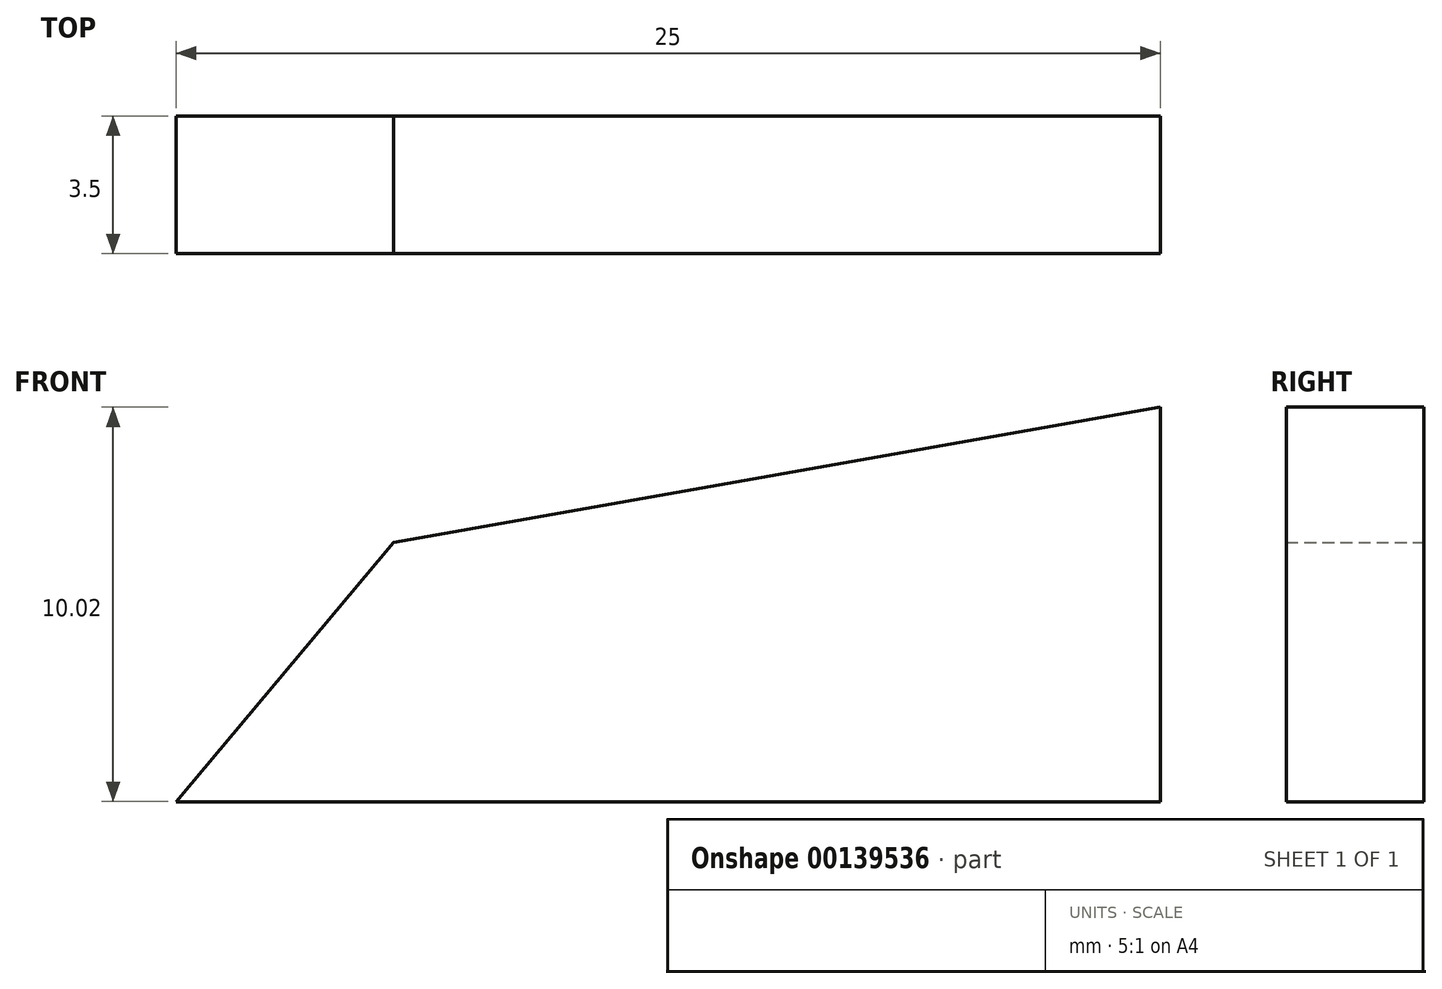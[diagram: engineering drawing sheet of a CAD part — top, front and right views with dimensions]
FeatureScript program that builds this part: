
annotation { "Feature Type Name" : "Feature", "Feature Type Description" : "" }
export const myFeature = defineFeature(function(context is Context, id is Id, definition is map)
    precondition{}
    {
        {
            var Q0;
            Q0=qCreatedBy(makeId("Front.planeOp"),FACE);
            var sketch = newSketch(context, id + "F0", { "sketchPlane" : qUnion([Q0])});
            skLineSegment(sketch, "E0", {"start": v(-31.3, -3.68) * mm, "end": v(-25.78, 2.9) * mm});
            skPoint(sketch, "E1.visualSharp", {"position": v(-31.3, -3.68) * mm});
            skLineSegment(sketch, "E2", {"start": v(-25.78, 2.9) * mm, "end": v(-2.15, 7.07) * mm});
            skLineSegment(sketch, "E3", {"start": v(-6.3, -3.68) * mm, "end": v(-6.3, 7.07) * mm});
            skLineSegment(sketch, "E4", {"start": v(-31.3, -3.68) * mm, "end": v(-6.3, -3.68) * mm});
            skSolve(sketch);
        }
        {
            var Q0;
            Q0 = qSketchRegion(id + "F0", true);
            var Q1;
            {var subQ0=sQuery(id+"F0.wireOp",EDGE,"E0");Q1=makeQuery(id+"F0.imprint","IMPRINT",FACE,{"disambiguationData":[TD([[makeQuery(id+"F0.imprint","IMPRINT",EDGE,{"derivedFrom":subQ0}),-1.0]])]});}
            extrude(context, id + "F1", {"entities" : qUnion([Q0, Q1]), "depth" : 3.5 * mm});
        }
    });
